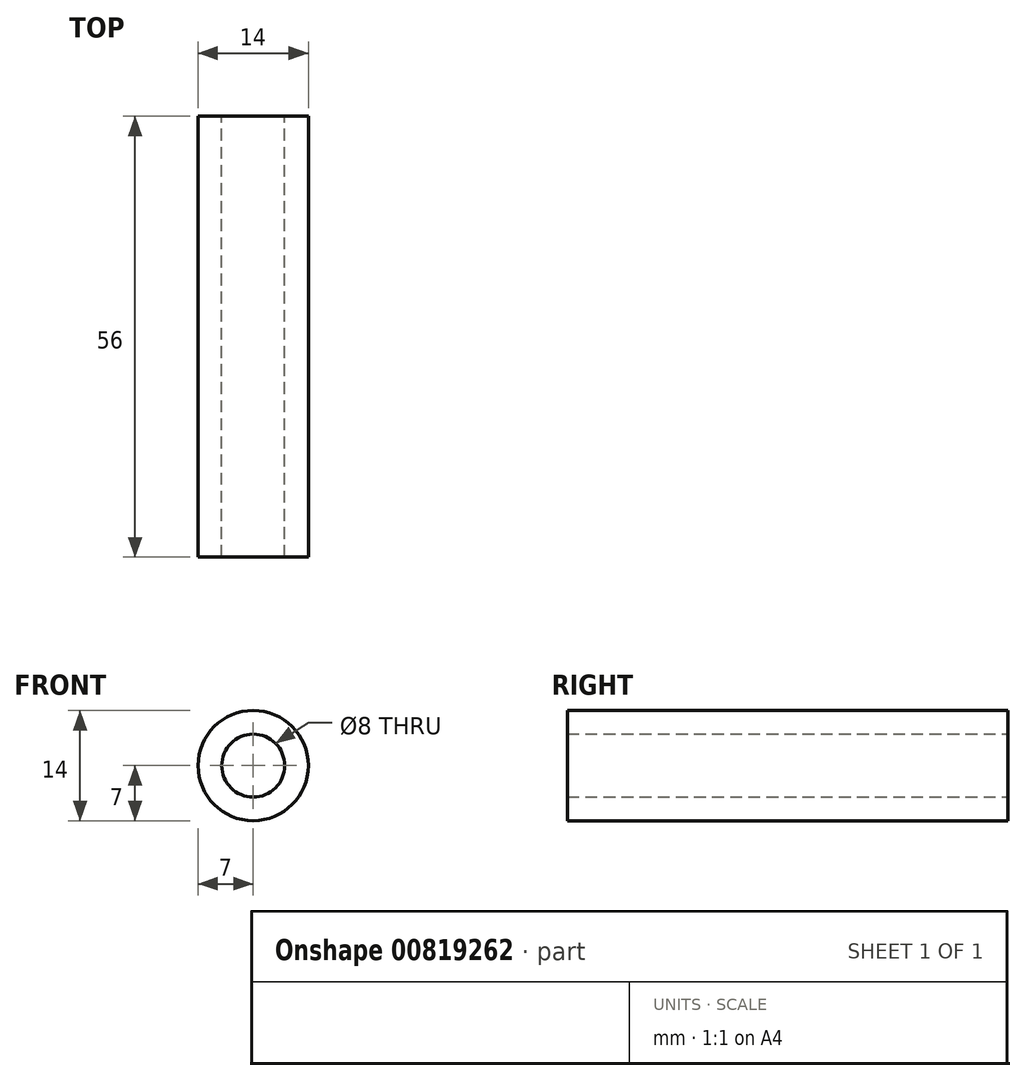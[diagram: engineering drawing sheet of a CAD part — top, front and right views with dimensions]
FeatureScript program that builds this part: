
annotation { "Feature Type Name" : "Feature", "Feature Type Description" : "" }
export const myFeature = defineFeature(function(context is Context, id is Id, definition is map)
    precondition{}
    {
        {
            var Q0;
            Q0=qCreatedBy(makeId("Front.planeOp"),FACE);
            var sketch = newSketch(context, id + "F0", { "sketchPlane" : qUnion([Q0])});
            skCircle(sketch, "E0", {"center": v(0, 0) * mm, "radius": 7 * mm});
            skCircle(sketch, "E1", {"center": v(0, 0) * mm, "radius": 4 * mm});
            skSolve(sketch);
        }
        {
            var Q0;
            Q0=makeQuery(id+"F0.imprint","IMPRINT",FACE,{"disambiguationData":[TD([[makeQuery(id+"F0.imprint","IMPRINT",EDGE,{"derivedFrom":sQuery(id+"F0.wireOp",EDGE,"E0")}),1.0]])]});
            extrude(context, id + "F1", {"entities" : qUnion([Q0]), "endBound" : BoundingType.SYMMETRIC, "depth" : 56 * mm, "offsetDistance" : 25 * mm});
        }
    });
